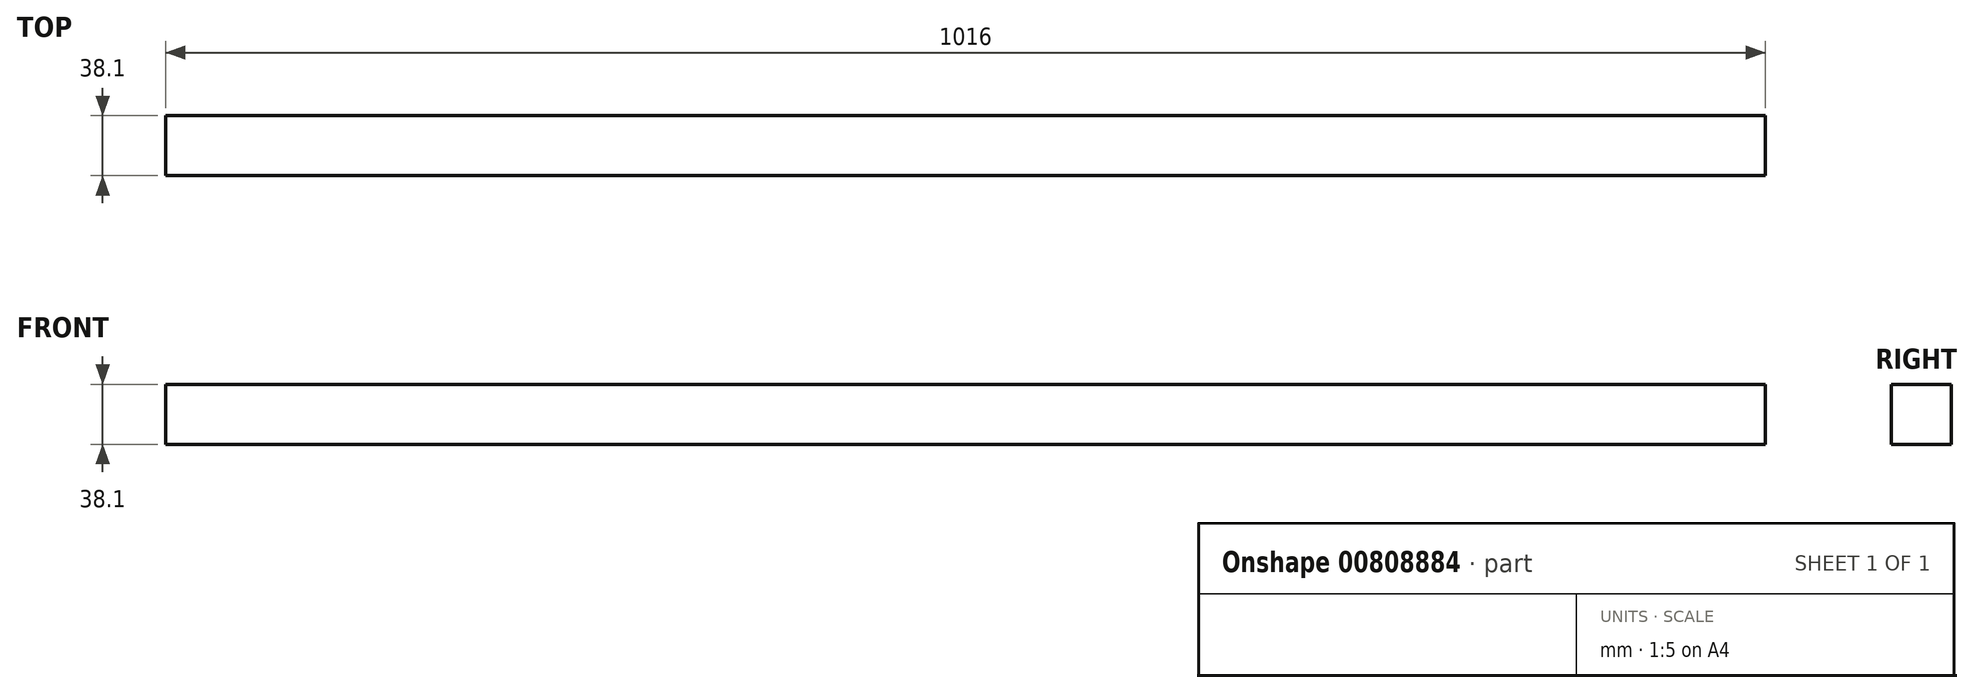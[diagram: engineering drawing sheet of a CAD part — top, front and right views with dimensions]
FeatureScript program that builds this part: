
annotation { "Feature Type Name" : "Feature", "Feature Type Description" : "" }
export const myFeature = defineFeature(function(context is Context, id is Id, definition is map)
    precondition{}
    {
        {
            var Q0;
            Q0=qCreatedBy(makeId("Top.planeOp"),FACE);
            var sketch = newSketch(context, id + "F0", { "sketchPlane" : qUnion([Q0])});
            skLineSegment(sketch, "E0.bottom", {"start": v(-616.3, 10.76) * mm, "end": v(399.7, 10.76) * mm});
            skLineSegment(sketch, "E0.top", {"start": v(-616.3, -27.34) * mm, "end": v(399.7, -27.34) * mm});
            skLineSegment(sketch, "E0.left", {"start": v(-616.3, 10.76) * mm, "end": v(-616.3, -27.34) * mm});
            skLineSegment(sketch, "E0.right", {"start": v(399.7, 10.76) * mm, "end": v(399.7, -27.34) * mm});
            skSolve(sketch);
        }
        {
            var Q0;
            Q0 = qSketchRegion(id + "F0", true);
            extrude(context, id + "F1", {"entities" : qUnion([Q0]), "depth" : 38.1 * mm, "offsetDistance" : 25.4 * mm});
        }
    });
